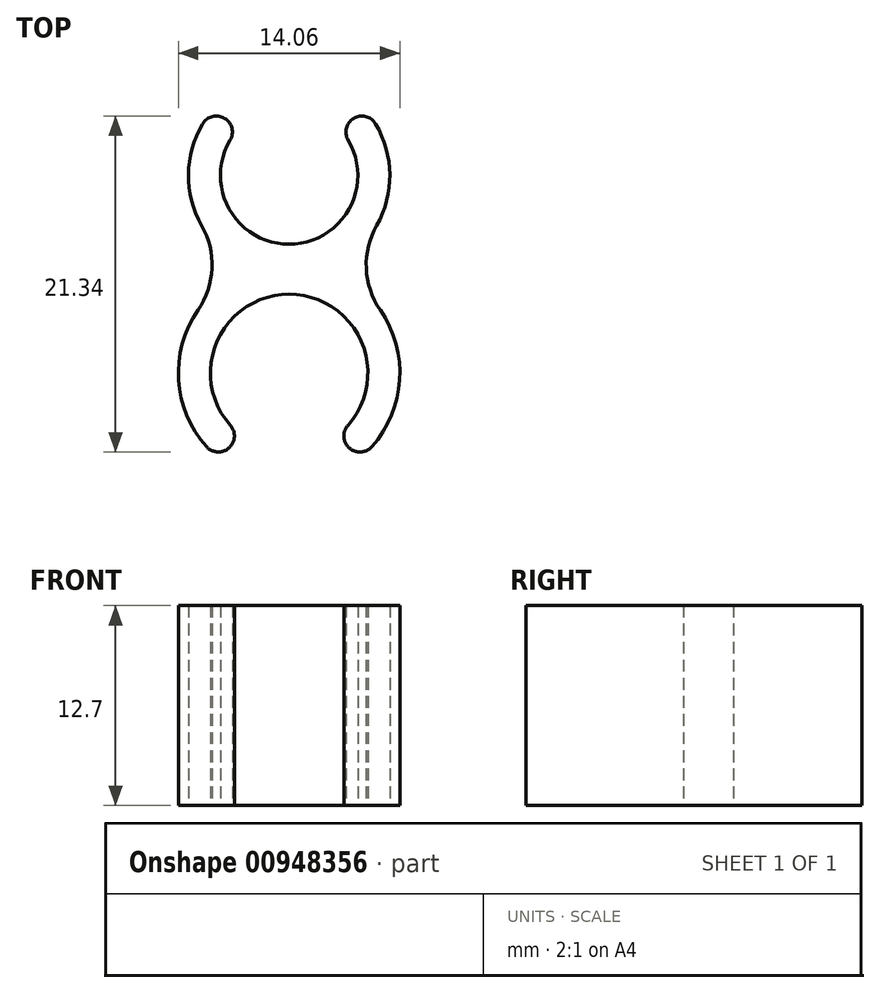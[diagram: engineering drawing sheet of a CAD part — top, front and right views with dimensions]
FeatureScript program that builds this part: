
annotation { "Feature Type Name" : "Feature", "Feature Type Description" : "" }
export const myFeature = defineFeature(function(context is Context, id is Id, definition is map)
    precondition{}
    {
        {
            var Q0;
            Q0=qCreatedBy(makeId("Top.planeOp"),FACE);
            var sketch = newSketch(context, id + "F0", { "sketchPlane" : qUnion([Q0])});
            skArc(sketch, "E0", {"start": v(3.73, -3.33) * mm, "mid": v(0, 5) * mm, "end": v(-3.73, -3.33) * mm});
            skArc(sketch, "E1", {"start": v(-3.75, 14.78) * mm, "mid": v(0, 8.17) * mm, "end": v(3.75, 14.78) * mm});
            skArc(sketch, "E2.0", {"start": v(5.56, 9.38) * mm, "mid": v(6.4, 12.6) * mm, "end": v(5.5, 15.82) * mm});
            skArc(sketch, "E3.0", {"start": v(-5.8, 3.99) * mm, "mid": v(-7.02, -0.44) * mm, "end": v(-5.25, -4.68) * mm});
            skArc(sketch, "E4.filletArc", {"start": v(5.56, 9.38) * mm, "mid": v(4.9, 6.65) * mm, "end": v(5.8, 3.99) * mm});
            skArc(sketch, "E5.filletArc", {"start": v(-5.8, 3.99) * mm, "mid": v(-4.9, 6.65) * mm, "end": v(-5.56, 9.38) * mm});
            skArc(sketch, "E6", {"start": v(5.5, 15.82) * mm, "mid": v(4.1, 16.17) * mm, "end": v(3.75, 14.78) * mm});
            skArc(sketch, "E7", {"start": v(-3.75, 14.78) * mm, "mid": v(-4.1, 16.17) * mm, "end": v(-5.5, 15.82) * mm});
            skArc(sketch, "E8", {"start": v(-5.25, -4.68) * mm, "mid": v(-3.82, -4.76) * mm, "end": v(-3.73, -3.33) * mm});
            skArc(sketch, "E9", {"start": v(3.73, -3.33) * mm, "mid": v(3.82, -4.76) * mm, "end": v(5.25, -4.68) * mm});
            skArc(sketch, "E10.trimOffspring", {"start": v(5.25, -4.68) * mm, "mid": v(7.02, -0.44) * mm, "end": v(5.8, 3.99) * mm});
            skArc(sketch, "E11.trimOffspring", {"start": v(-5.5, 15.82) * mm, "mid": v(-6.4, 12.6) * mm, "end": v(-5.56, 9.38) * mm});
            skLineSegment(sketch, "E12", {"start": v(-4.37, 12.54) * mm, "end": v(-4.37, 21.58) * mm, "construction": true});
            skLineSegment(sketch, "E13", {"start": v(-5, 0) * mm, "end": v(-5, -9.17) * mm, "construction": true});
            skSolve(sketch);
        }
        {
            var Q0;
            Q0 = qSketchRegion(id + "F0", true);
            extrude(context, id + "F1", {"entities" : qUnion([Q0]), "depth" : 12.7 * mm, "offsetDistance" : 25.4 * mm});
        }
    });
